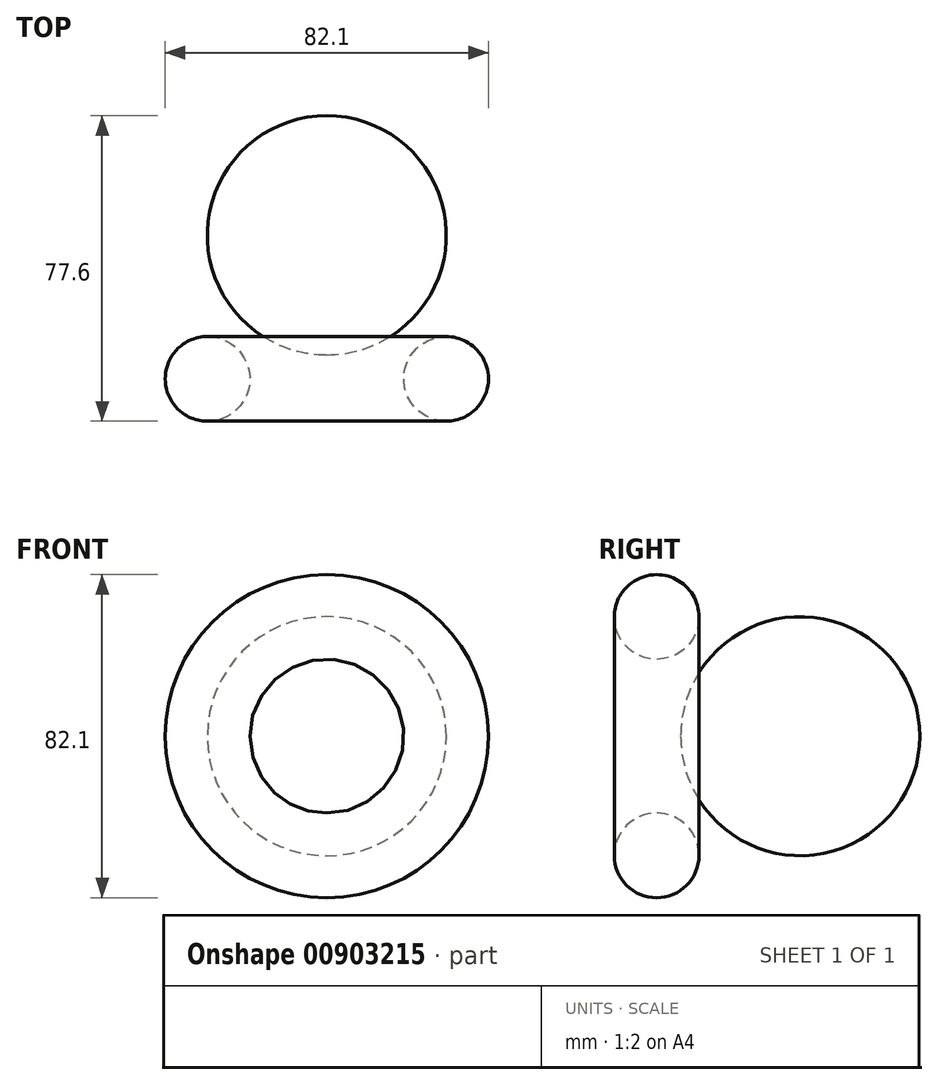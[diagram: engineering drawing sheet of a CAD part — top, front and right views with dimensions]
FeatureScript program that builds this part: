
annotation { "Feature Type Name" : "Feature", "Feature Type Description" : "" }
export const myFeature = defineFeature(function(context is Context, id is Id, definition is map)
    precondition{}
    {
        {
            var Q0;
            Q0=qCreatedBy(makeId("Top.planeOp"),FACE);
            var sketch = newSketch(context, id + "F0", { "sketchPlane" : qUnion([Q0])});
            skCircle(sketch, "E0", {"center": v(0, 0) * mm, "radius": 30.37 * mm});
            skPoint(sketch, "E1", {"position": v(0, -30.37) * mm});
            skSolve(sketch);
        }
        {
            var Q0;
            Q0=qCreatedBy(makeId("Front.planeOp"),FACE);
            var sketch = newSketch(context, id + "F1", { "sketchPlane" : qUnion([Q0])});
            skCircle(sketch, "E2", {"center": v(0, 0) * mm, "radius": 19 * mm});
            skSolve(sketch);
        }
        {
            var Q0;
            Q0=makeQuery(id+"F0.imprint","IMPRINT",FACE,{"disambiguationData":[TD([[makeQuery(id+"F0.imprint","IMPRINT",EDGE,{"derivedFrom":sQuery(id+"F0.wireOp",EDGE,"E0")}),1.0]])]});
            var Q1;
            Q1=sQuery(id+"F1.wireOp",EDGE,"E2");
            sweep(context, id + "F2", {"profiles" : qUnion([Q0]), "path" : qUnion([Q1])});
        }
        {
            var Q0;
            Q0=qCreatedBy(makeId("Top.planeOp"),FACE);
            var sketch = newSketch(context, id + "F3", { "sketchPlane" : qUnion([Q0])});
            skCircle(sketch, "E3", {"center": v(30.3, -36.48) * mm, "radius": 10.76 * mm});
            skPoint(sketch, "E4", {"position": v(37.8, -28.76) * mm});
            skSolve(sketch);
        }
        {
            var Q0;
            Q0=makeQuery(id+"F3.imprint","IMPRINT",FACE,{"disambiguationData":[TD([[makeQuery(id+"F3.imprint","IMPRINT",EDGE,{"derivedFrom":sQuery(id+"F3.wireOp",EDGE,"E3")}),1.0]])]});
            var Q1;
            Q1 = qConstructionFilter(qBodyType(qCreatedBy(id + "F1" ,EDGE), BodyType.WIRE), ConstructionObject.NO);
            sweep(context, id + "F4", {"profiles" : qUnion([Q0]), "path" : qUnion([Q1])});
        }
    });
